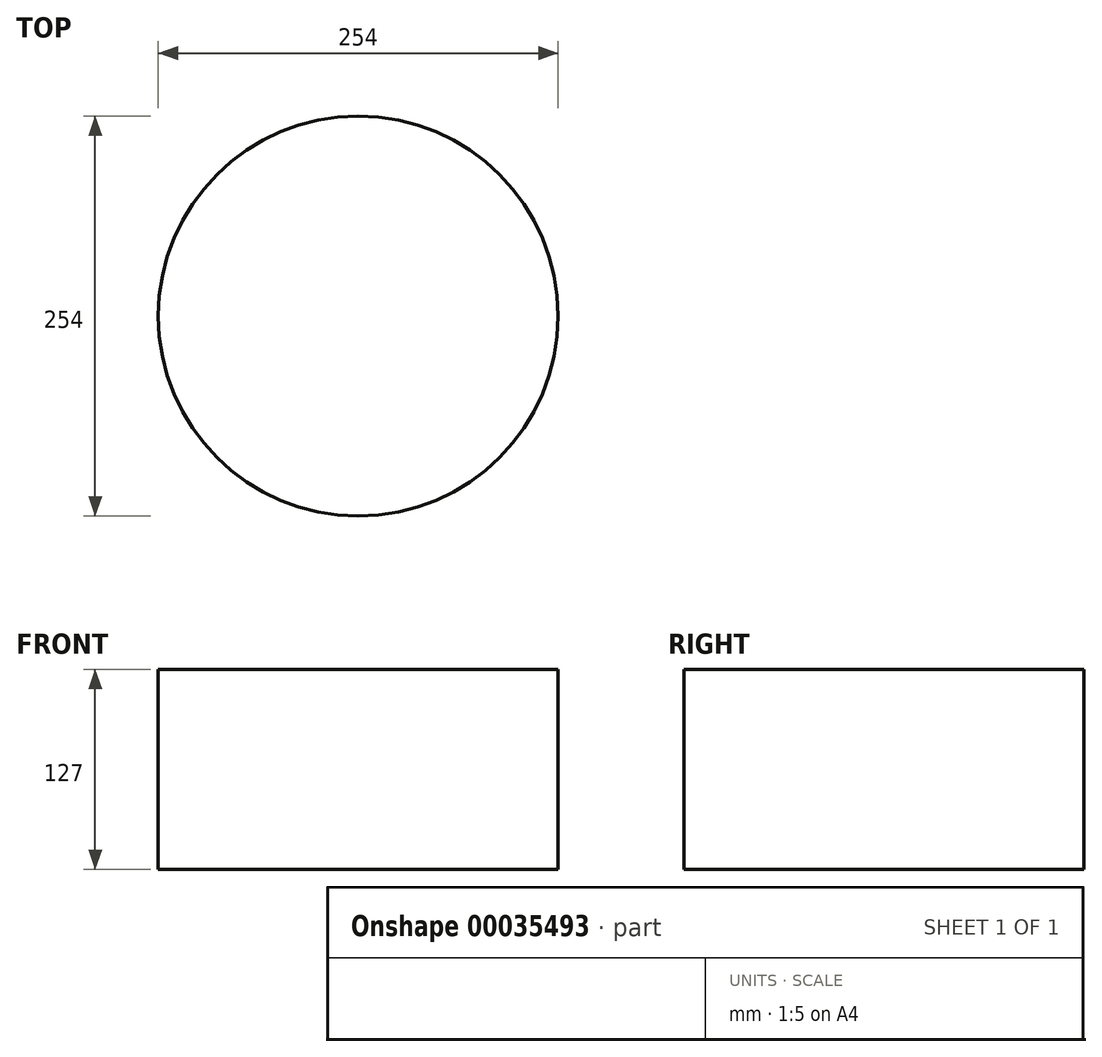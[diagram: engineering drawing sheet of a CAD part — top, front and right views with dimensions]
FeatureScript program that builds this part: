
annotation { "Feature Type Name" : "Feature", "Feature Type Description" : "" }
export const myFeature = defineFeature(function(context is Context, id is Id, definition is map)
    precondition{}
    {
        {
            var Q0;
            Q0=qCreatedBy(makeId("Top.planeOp"),FACE);
            var sketch = newSketch(context, id + "F0", { "sketchPlane" : qUnion([Q0])});
            skCircle(sketch, "E0", {"center": v(0, 0) * mm, "radius": 127 * mm});
            skSolve(sketch);
        }
        {
            var Q0;
            Q0=makeQuery(id+"F0.imprint","IMPRINT",FACE,{"disambiguationData":[TD([[makeQuery(id+"F0.imprint","IMPRINT",EDGE,{"derivedFrom":sQuery(id+"F0.wireOp",EDGE,"E0")}),1.0]])]});
            extrude(context, id + "F1", {"entities" : qUnion([Q0]), "endBound" : BoundingType.SYMMETRIC, "depth" : 127 * mm});
        }
    });
